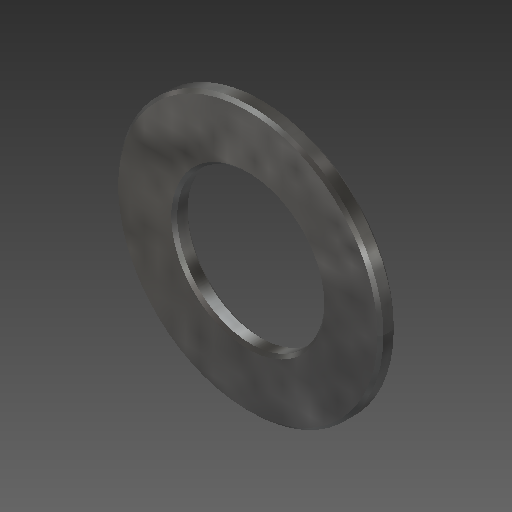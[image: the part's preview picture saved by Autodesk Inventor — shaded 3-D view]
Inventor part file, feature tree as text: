
AUTODESK INVENTOR PART (.ipt)
format: ipt  version: 2018 (Build 220112000, 112)  size: 136,192 bytes
history: native  units: mm
features: extrude x1, chamfer x1, sketch x1
ambient origin geometry x8: Origin, YZ Plane, XZ Plane, XY Plane, X Axis, Y Axis, Z Axis, Center Point
bodies: Solid1 (feature_tree)
feature tree (3):
  extrude  "Extrusion1"  Depth=1.1mm
  chamfer  "Chamfer1"  Distance=1.1mm
  sketch  "Sketch1"  dims[d0=10.0mm d1=18.0mm d2=1.1mm d3=0.0mm d4=0.2mm d5=2.0mm d6=45.0deg]
